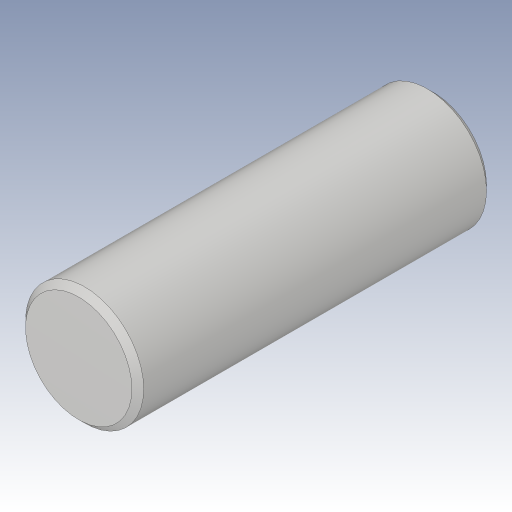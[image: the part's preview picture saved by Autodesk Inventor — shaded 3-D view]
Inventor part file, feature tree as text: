
AUTODESK INVENTOR PART (.ipt)
format: ipt  version: 2023.3 (Build 273359000, 359)  size: 138,240 bytes
history: native  units: in
note: dims shown in document units (in); Inventor stores cm internally (conversion verified against a paired STEP export)
features: extrude x1, chamfer x1, sketch x1
ambient origin geometry x8: Origin, YZ Plane, XZ Plane, XY Plane, X Axis, Y Axis, Z Axis, Center Point
bodies: Body1 (feature_tree)
feature tree (3):
  extrude  "Extrusion3"  Depth=0.7087in TaperAngle=0.0deg
  chamfer  "Fase1"  Distance=0.0118in Angle=45.0deg
  sketch  "Skizze3"  dims[d4=0.2362in d5=0.7087in d6=0.0in d7=0.0118in d8=0.0787in d9=45.0deg]
